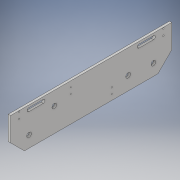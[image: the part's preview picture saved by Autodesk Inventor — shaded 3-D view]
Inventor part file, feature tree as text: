
AUTODESK INVENTOR PART (.ipt)
format: ipt  version: 2017 (Build 210142000, 142)  size: 201,728 bytes
history: native  units: in
note: dims shown in document units (in); Inventor stores cm internally (conversion verified against a paired STEP export)
features: extrude x5, sketch x5, projected_geometry x4, chamfer x2
ambient origin geometry x8: Origin, YZ Plane, XZ Plane, XY Plane, X Axis, Y Axis, Z Axis, Center Point
bodies: Solid1 (feature_tree)
feature tree (16):
  extrude  "Extrusion1"  Depth=17.5in
  chamfer  "Chamfer1"  Distance=0.25in
  chamfer  "Chamfer2"  Distance=1.5in Angle=45.0deg
  extrude  "Extrusion2"  Depth=0.375in TaperAngle=45.0deg
  extrude  "Extrusion3"  Depth=0.375in
  extrude  "Extrusion4"  Depth=0.375in
  extrude  "Extrusion5"  Depth=0.375in
  sketch  "Sketch1"  dims[d0=4.07in d1=17.5in]
  sketch  "Sketch2"  dims[d2=0.501in]
  projected_geometry  "Projected Loop1"
  sketch  "Sketch3"  dims[d3=1.25in]
  projected_geometry  "Projected Loop2"
  sketch  "Sketch4"  dims[d4=2.0in]
  projected_geometry  "Projected Loop3"
  sketch  "Sketch5"  dims[d5=2.0in d6=0.25in d7=0.0in d8=1.5in d9=0.125in d10=45.0deg d11=1.5in d12=0.125in d13=45.0deg d14=0.501in d15=4.741in d16=1.469in d17=0.501in d18=1.469in d19=4.741in d20=1.0in d21=0.0in d22=6.517in d23=0.125in d24=0.603in d25=0.125in d26=0.63in d27=6.517in d28=0.125in d29=0.603in d30=6.517in d31=0.125in d32=0.63in d33=6.517in d34=0.125in d35=6.517in d36=0.603in d37=0.125in d38=0.63in d39=0.125in d40=0.125in d41=0.603in d42=0.63in d43=6.517in d44=1.0in d45=0.0in d46=0.375in d47=1.975in d48=0.438in d49=0.375in d50=1.575in d57=1.0in d58=0.0in d59=0.155in d60=0.906in d61=0.094in d62=0.155in d64=0.155in d65=0.155in d66=0.094in d68=0.904in d69=1.0in d70=0.0in d71=0.781in d72=0.781in d73=0.375in d74=0.375in d75=1.975in d76=1.575in d77=0.438in]
  projected_geometry  "Projected Loop4"
